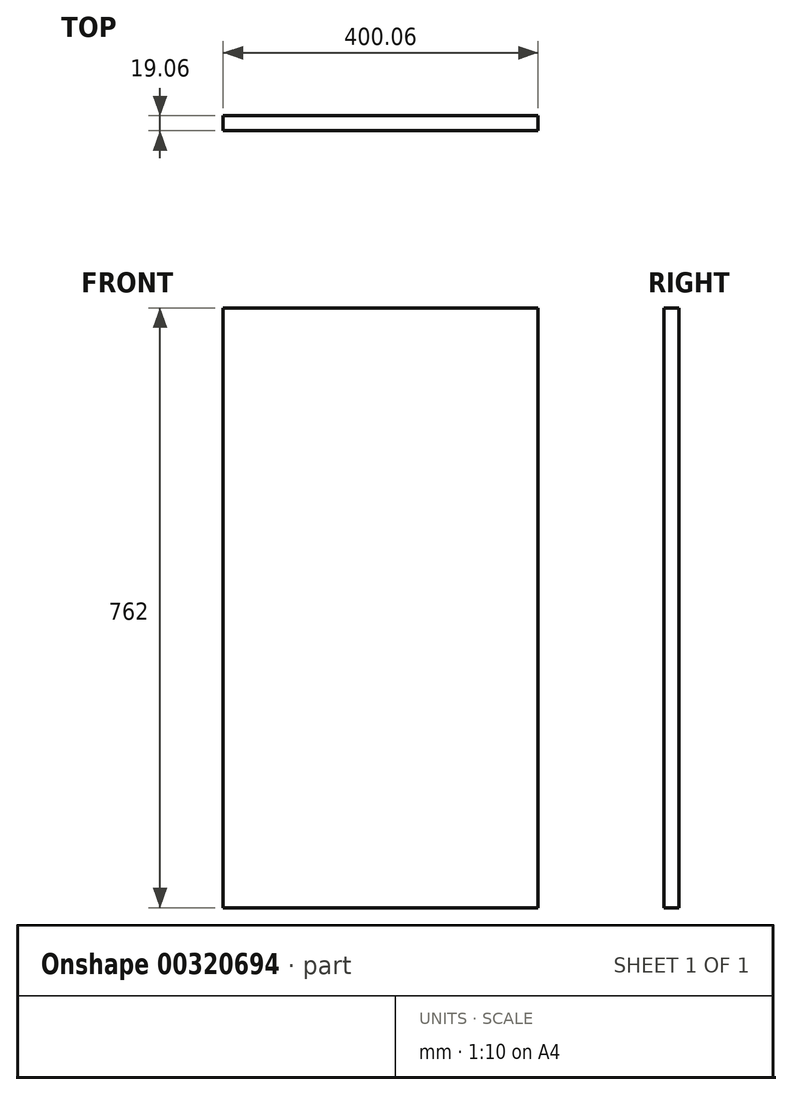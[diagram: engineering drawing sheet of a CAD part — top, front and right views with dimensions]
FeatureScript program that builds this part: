
annotation { "Feature Type Name" : "Feature", "Feature Type Description" : "" }
export const myFeature = defineFeature(function(context is Context, id is Id, definition is map)
    precondition{}
    {
        {
            var Q0;
            Q0=qCreatedBy(makeId("Front.planeOp"),FACE);
            var sketch = newSketch(context, id + "F0", { "sketchPlane" : qUnion([Q0])});
            skLineSegment(sketch, "E0.bottom", {"start": v(-200.03, 381) * mm, "end": v(200.03, 381) * mm});
            skLineSegment(sketch, "E0.top", {"start": v(-200.03, -381) * mm, "end": v(200.03, -381) * mm});
            skLineSegment(sketch, "E0.left", {"start": v(-200.03, 381) * mm, "end": v(-200.03, -381) * mm});
            skLineSegment(sketch, "E0.right", {"start": v(200.03, 381) * mm, "end": v(200.03, -381) * mm});
            skPoint(sketch, "E0.middle", {"position": v(0, 0) * mm});
            skSolve(sketch);
        }
        {
            var Q0;
            Q0 = qSketchRegion(id + "F0", true);
            extrude(context, id + "F1", {"entities" : qUnion([Q0]), "depth" : 19.05 * mm, "symmetric" : true});
        }
    });
